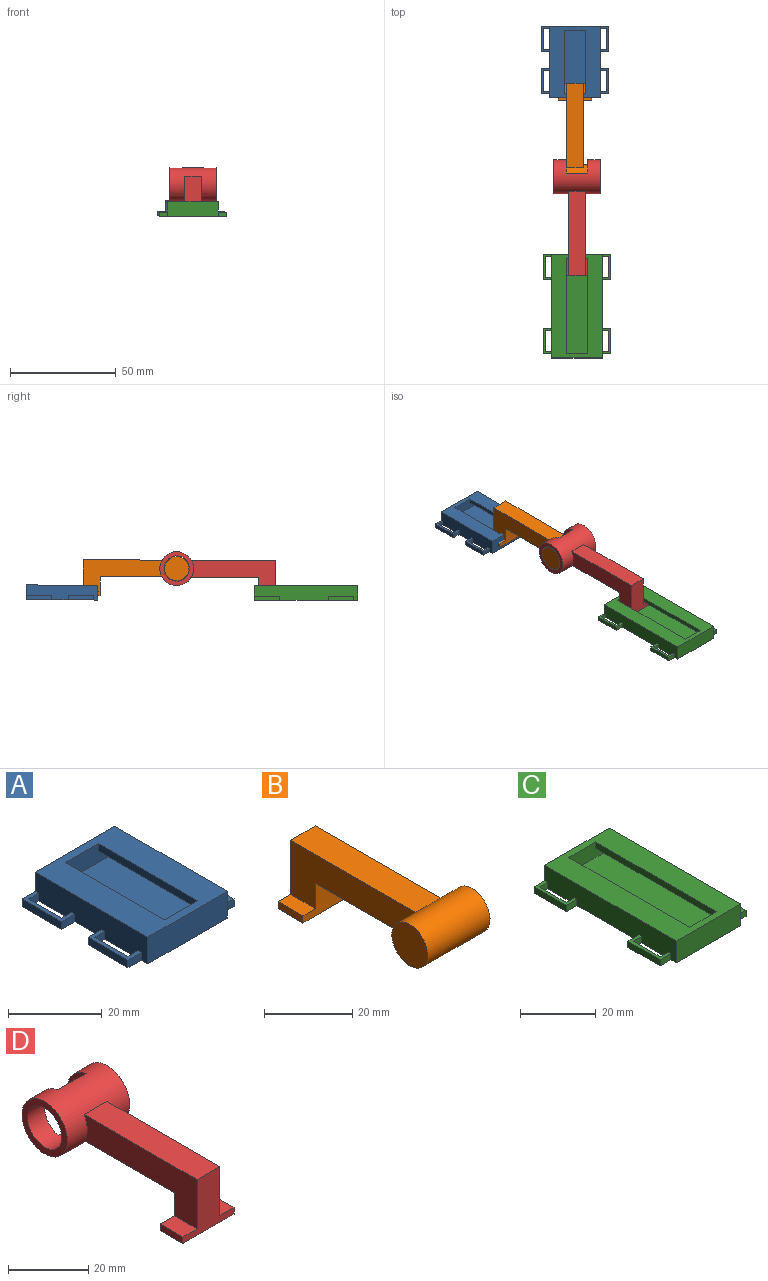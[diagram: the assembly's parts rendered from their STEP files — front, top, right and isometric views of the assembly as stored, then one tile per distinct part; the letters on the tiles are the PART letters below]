
ASSEMBLY  parts=4 mates=3
PART A: 41 faces, bbox 32x34x7 mm
  f0: plane 34x24mm, normal (0,0,1), area 516mm2, adj f1,f3,f4,f5,f7,f8,f15,f16
  f1: plane 34x7mm, normal (-1,0,0), area 230mm2, adj f0,f2,f4,f9,f15,f17,f19,f20
  f2: plane 34x32mm, normal (0,0,-1), area 888mm2, adj f1,f3,f4,f6,f9,f15,f17,f18
  f3: plane 34x7mm, normal (1,0,0), area 230mm2, adj f0,f2,f4,f6,f15,f23,f25,f26
  f4: plane 24x7mm, normal (0,-1,0), area 168mm2, adj f0,f1,f2,f3
  f5: plane 20x5mm, normal (0,1,0), area 80mm2, adj f0,f7,f8,f10,f11,f12,f13,f14
  f6: plane 4x2mm, normal (0,-1,0), area 8mm2, adj f2,f3,f39,f40
  f7: plane 30x2mm, normal (-1,0,0), area 60mm2, adj f0,f5,f11,f16
  f8: plane 30x2mm, normal (1,0,0), area 60mm2, adj f0,f5,f13,f16
  f9: plane 4x2mm, normal (0,-1,0), area 8mm2, adj f1,f2,f33,f34
  f10: plane 30x3mm, normal (-1,0,0), area 90mm2, adj f5,f11,f14,f16
  f11: plane 30x5mm, normal (0,0,-1), area 150mm2, adj f5,f7,f10,f16
  f12: plane 30x3mm, normal (1,0,0), area 90mm2, adj f5,f13,f14,f16
  f13: plane 30x5mm, normal (0,0,-1), area 150mm2, adj f5,f8,f12,f16
  f14: plane 30x20mm, normal (0,0,1), area 600mm2, adj f5,f10,f12,f16
  f15: plane 32x7mm, normal (0,1,0), area 184mm2, adj f0,f1,f2,f3,f21,f22,f27,f28
  f16: plane 20x5mm, normal (0,-1,0), area 80mm2, adj f0,f7,f8,f10,f11,f12,f13,f14
  f17: plane 3x2mm, normal (0,-1,0), area 6mm2, adj f1,f2,f18,f22
  f18: plane 10x2mm, normal (1,0,0), area 20mm2, adj f2,f17,f19,f22
  f19: plane 3x2mm, normal (0,1,0), area 6mm2, adj f1,f2,f18,f22
  f20: plane 4x2mm, normal (0,-1,0), area 8mm2, adj f1,f2,f21,f22
  f21: plane 12x2mm, normal (-1,0,0), area 24mm2, adj f2,f15,f20,f22
  f22: plane 12x4mm, normal (0,0,1), area 18mm2, adj f1,f15,f17,f18,f19,f20,f21
  f23: plane 3x2mm, normal (0,-1,0), area 6mm2, adj f2,f3,f24,f28
  f24: plane 10x2mm, normal (-1,0,0), area 20mm2, adj f2,f23,f25,f28
  f25: plane 3x2mm, normal (0,1,0), area 6mm2, adj f2,f3,f24,f28
  f26: plane 4x2mm, normal (0,-1,0), area 8mm2, adj f2,f3,f27,f28
  f27: plane 12x2mm, normal (1,0,0), area 24mm2, adj f2,f15,f26,f28
  f28: plane 12x4mm, normal (0,0,1), area 18mm2, adj f3,f15,f23,f24,f25,f26,f27
  f29: plane 3x2mm, normal (0,1,0), area 6mm2, adj f1,f2,f30,f34
  f30: plane 10x2mm, normal (1,0,0), area 20mm2, adj f2,f29,f31,f34
  f31: plane 3x2mm, normal (0,-1,0), area 6mm2, adj f1,f2,f30,f34
  f32: plane 4x2mm, normal (0,1,0), area 8mm2, adj f1,f2,f33,f34
  f33: plane 12x2mm, normal (-1,0,0), area 24mm2, adj f2,f9,f32,f34
  f34: plane 12x4mm, normal (0,0,1), area 18mm2, adj f1,f9,f29,f30,f31,f32,f33
  f35: plane 3x2mm, normal (0,1,0), area 6mm2, adj f2,f3,f36,f40
  f36: plane 10x2mm, normal (-1,0,0), area 20mm2, adj f2,f35,f37,f40
  f37: plane 3x2mm, normal (0,-1,0), area 6mm2, adj f2,f3,f36,f40
  f38: plane 4x2mm, normal (0,1,0), area 8mm2, adj f2,f3,f39,f40
  f39: plane 12x2mm, normal (1,0,0), area 24mm2, adj f2,f6,f38,f40
  f40: plane 12x4mm, normal (0,0,1), area 18mm2, adj f3,f6,f35,f36,f37,f38,f39
PART B: 14 faces, bbox 20x50x18.8 mm
  f0: cylinder r=5.75mm len=20mm, axis (-1,0,0), area 651.8mm2, adj f1,f2,f3,f4,f6,f8
  f1: plane 11.5x11.5mm, normal (1,0,0), area 103.9mm2, adj f0
  f2: plane 11.5x11.5mm, normal (-1,0,0), area 103.9mm2, adj f0
  f3: plane 40.12x8mm, normal (0,0,1), area 321mm2, adj f0,f6,f7,f8
  f4: plane 32.12x8mm, normal (0,0,-1), area 257mm2, adj f0,f5,f6,f8
  f5: plane 16x9mm, normal (0,-1,0), area 88mm2, adj f4,f6,f8,f9,f10,f11,f12,f13
  f6: plane 40.12x15mm, normal (1,0,0), area 368mm2, adj f0,f3,f4,f5,f7,f9
  f7: plane 17x16mm, normal (0,1,0), area 152mm2, adj f3,f6,f8,f9,f10,f11,f12,f13
  f8: plane 40.12x15mm, normal (-1,0,0), area 368mm2, adj f0,f3,f4,f5,f7,f13
  f9: plane 8x4mm, normal (0,0,1), area 32mm2, adj f5,f6,f7,f10
  f10: plane 8x2mm, normal (1,0,0), area 16mm2, adj f5,f7,f9,f12
  f11: plane 8x2mm, normal (-1,0,0), area 16mm2, adj f5,f7,f12,f13
  f12: plane 16x8mm, normal (0,0,-1), area 128mm2, adj f5,f7,f10,f11
  f13: plane 8x4mm, normal (0,0,1), area 32mm2, adj f5,f7,f8,f11
PART C: 41 faces, bbox 32x49x7 mm
  f0: plane 49x24mm, normal (0,0,1), area 726mm2, adj f1,f3,f4,f5,f7,f8,f15,f16
  f1: plane 49x7mm, normal (-1,0,0), area 335mm2, adj f0,f2,f4,f9,f15,f17,f19,f20
  f2: plane 49x32mm, normal (0,0,-1), area 1248mm2, adj f1,f3,f4,f6,f9,f15,f17,f18
  f3: plane 49x7mm, normal (1,0,0), area 335mm2, adj f0,f2,f4,f6,f15,f23,f25,f26
  f4: plane 24x7mm, normal (0,-1,0), area 168mm2, adj f0,f1,f2,f3
  f5: plane 20x5mm, normal (0,1,0), area 80mm2, adj f0,f7,f8,f10,f11,f12,f13,f14
  f6: plane 4x2mm, normal (0,-1,0), area 8mm2, adj f2,f3,f39,f40
  f7: plane 45x2mm, normal (-1,0,0), area 90mm2, adj f0,f5,f11,f16
  f8: plane 45x2mm, normal (1,0,0), area 90mm2, adj f0,f5,f13,f16
  f9: plane 4x2mm, normal (0,-1,0), area 8mm2, adj f1,f2,f33,f34
  f10: plane 45x3mm, normal (-1,0,0), area 135mm2, adj f5,f11,f14,f16
  f11: plane 45x5mm, normal (0,0,-1), area 225mm2, adj f5,f7,f10,f16
  f12: plane 45x3mm, normal (1,0,0), area 135mm2, adj f5,f13,f14,f16
  f13: plane 45x5mm, normal (0,0,-1), area 225mm2, adj f5,f8,f12,f16
  f14: plane 45x20mm, normal (0,0,1), area 900mm2, adj f5,f10,f12,f16
  f15: plane 32x7mm, normal (0,1,0), area 184mm2, adj f0,f1,f2,f3,f21,f22,f27,f28
  f16: plane 20x5mm, normal (0,-1,0), area 80mm2, adj f0,f7,f8,f10,f11,f12,f13,f14
  f17: plane 3x2mm, normal (0,-1,0), area 6mm2, adj f1,f2,f18,f22
  f18: plane 10x2mm, normal (1,0,0), area 20mm2, adj f2,f17,f19,f22
  f19: plane 3x2mm, normal (0,1,0), area 6mm2, adj f1,f2,f18,f22
  f20: plane 4x2mm, normal (0,-1,0), area 8mm2, adj f1,f2,f21,f22
  f21: plane 12x2mm, normal (-1,0,0), area 24mm2, adj f2,f15,f20,f22
  f22: plane 12x4mm, normal (0,0,1), area 18mm2, adj f1,f15,f17,f18,f19,f20,f21
  f23: plane 3x2mm, normal (0,-1,0), area 6mm2, adj f2,f3,f24,f28
  f24: plane 10x2mm, normal (-1,0,0), area 20mm2, adj f2,f23,f25,f28
  f25: plane 3x2mm, normal (0,1,0), area 6mm2, adj f2,f3,f24,f28
  f26: plane 4x2mm, normal (0,-1,0), area 8mm2, adj f2,f3,f27,f28
  f27: plane 12x2mm, normal (1,0,0), area 24mm2, adj f2,f15,f26,f28
  f28: plane 12x4mm, normal (0,0,1), area 18mm2, adj f3,f15,f23,f24,f25,f26,f27
  f29: plane 3x2mm, normal (0,1,0), area 6mm2, adj f1,f2,f30,f34
  f30: plane 10x2mm, normal (1,0,0), area 20mm2, adj f2,f29,f31,f34
  f31: plane 3x2mm, normal (0,-1,0), area 6mm2, adj f1,f2,f30,f34
  f32: plane 4x2mm, normal (0,1,0), area 8mm2, adj f1,f2,f33,f34
  f33: plane 12x2mm, normal (-1,0,0), area 24mm2, adj f2,f9,f32,f34
  f34: plane 12x4mm, normal (0,0,1), area 18mm2, adj f1,f9,f29,f30,f31,f32,f33
  f35: plane 3x2mm, normal (0,1,0), area 6mm2, adj f2,f3,f36,f40
  f36: plane 10x2mm, normal (-1,0,0), area 20mm2, adj f2,f35,f37,f40
  f37: plane 3x2mm, normal (0,-1,0), area 6mm2, adj f2,f3,f36,f40
  f38: plane 4x2mm, normal (0,1,0), area 8mm2, adj f2,f3,f39,f40
  f39: plane 12x2mm, normal (1,0,0), area 24mm2, adj f2,f6,f38,f40
  f40: plane 12x4mm, normal (0,0,1), area 18mm2, adj f3,f6,f35,f36,f37,f38,f39
PART D: 19 faces, bbox 22x54.8x21 mm
  f0: plane 31.82x8mm, normal (0,0,-1), area 254.6mm2, adj f3,f10,f11,f13
  f1: plane 16x16mm, normal (-1,0,0), area 88mm2, adj f3,f4
  f2: plane 16x16mm, normal (1,0,0), area 88mm2, adj f3,f4
  f3: cylinder r=8mm len=22mm, axis (1,0,0), area 815.4mm2, adj f0,f1,f2,f5,f6,f7,f8,f9
  f4: cylinder r=6mm len=22mm, axis (1,0,0), area 661.8mm2, adj f1,f2,f5,f6,f7,f8
  f5: plane 15.76x6.96mm, normal (1,0,0), area 39.1mm2, adj f3,f4,f7,f8
  f6: plane 15.76x6.96mm, normal (-1,0,0), area 39.1mm2, adj f3,f4,f7,f8
  f7: plane 10x1.97mm, normal (0,0.98,-0.17), area 20mm2, adj f3,f4,f5,f6
  f8: plane 10x1.97mm, normal (0,0.98,0.17), area 20mm2, adj f3,f4,f5,f6
  f9: plane 39.82x8mm, normal (0,0,1), area 318.6mm2, adj f3,f10,f11,f12
  f10: plane 39.82x15mm, normal (-1,0,0), area 368.8mm2, adj f0,f3,f9,f12,f13,f14
  f11: plane 39.82x15mm, normal (1,0,0), area 368.8mm2, adj f0,f3,f9,f12,f13,f18
  f12: plane 18x17mm, normal (0,-1,0), area 156mm2, adj f9,f10,f11,f14,f15,f16,f17,f18
  f13: plane 18x9mm, normal (0,1,0), area 92mm2, adj f0,f10,f11,f14,f15,f16,f17,f18
  f14: plane 8x5mm, normal (0,0,1), area 40mm2, adj f10,f12,f13,f16
  f15: plane 8x2mm, normal (1,0,0), area 16mm2, adj f12,f13,f17,f18
  f16: plane 8x2mm, normal (-1,0,0), area 16mm2, adj f12,f13,f14,f17
  f17: plane 18x8mm, normal (0,0,-1), area 144mm2, adj f12,f13,f15,f16
  f18: plane 8x5mm, normal (0,0,1), area 40mm2, adj f11,f12,f13,f15
PLACE A rot(axis=(1,0,0),0.2deg) t=(43.48,12.94,-0.68)mm
PLACE B rot(axis=(1,0,0),0.2deg) t=(43.48,-16.07,1.22)mm
PLACE C t=(44.48,-95.11,-0.92)mm fixed
PLACE D t=(44.48,-16.11,1.08)mm
MATE slider C.f16 <-> D.f13  axis (0,-1,0) through (44.48,-95.11,-0.92)mm
MATE revolute B.f0 <-> D.f3  axis (-1,0,0) through (33.48,-56.36,12.08)mm
MATE slider B.f7 <-> A.f16  axis (0,1,0) through (43.48,-12.06,-0.77)mm
